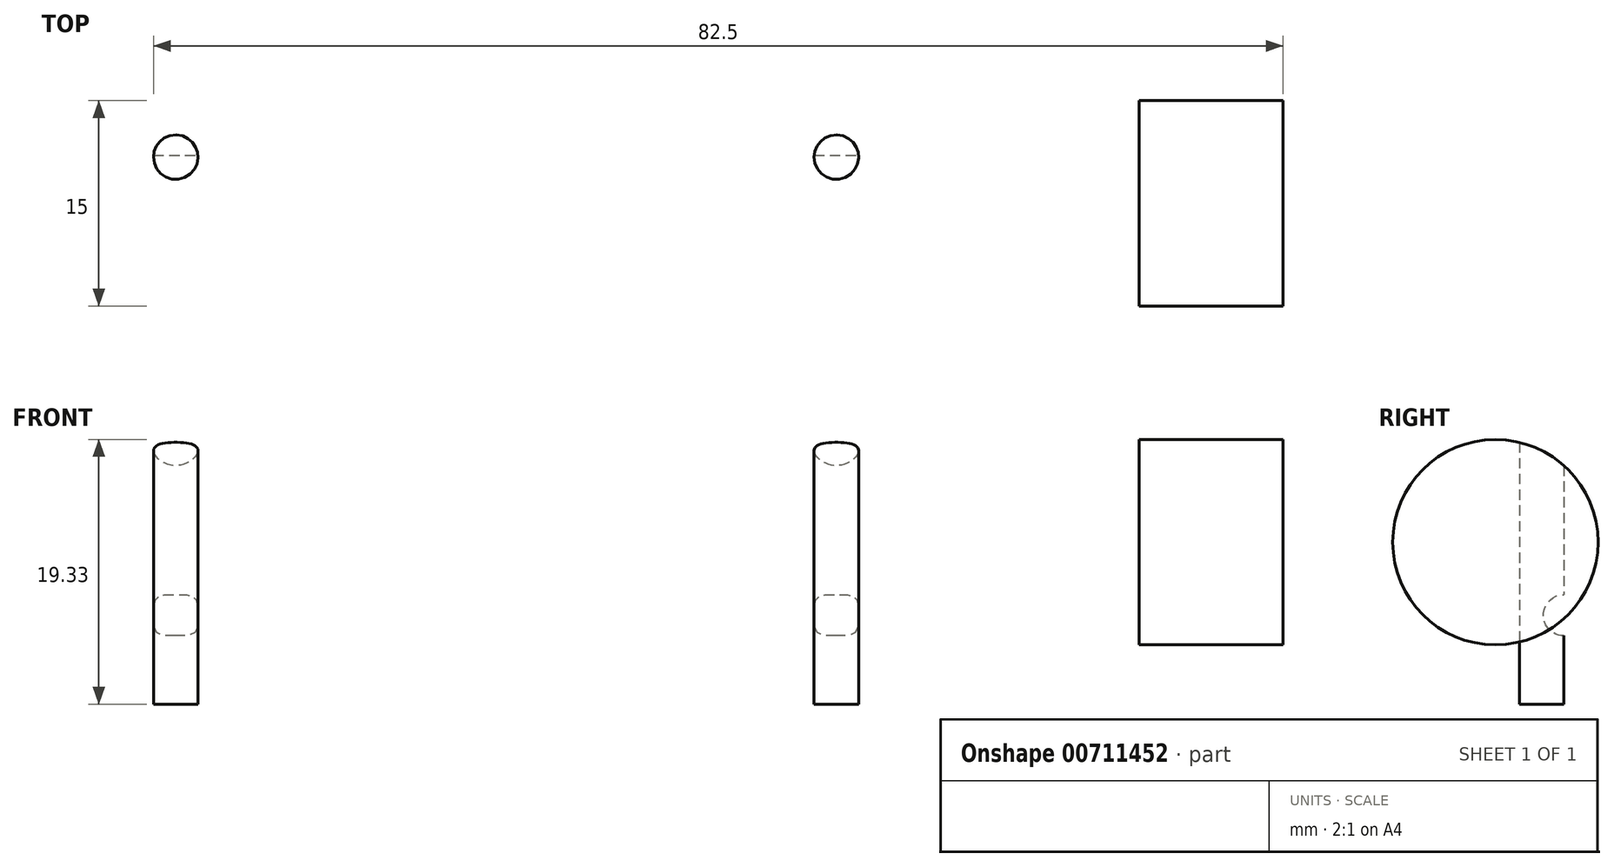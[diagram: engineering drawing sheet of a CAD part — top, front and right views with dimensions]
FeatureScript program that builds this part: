
annotation { "Feature Type Name" : "Feature", "Feature Type Description" : "" }
export const myFeature = defineFeature(function(context is Context, id is Id, definition is map)
    precondition{}
    {
        {
            var Q0;
            Q0=qCreatedBy(makeId("Top.planeOp"),FACE);
            var sketch = newSketch(context, id + "F0", { "sketchPlane" : qUnion([Q0])});
            skLineSegment(sketch, "E0.bottom", {"start": v(-41.74, -4.4) * mm, "end": v(51.26, -4.4) * mm});
            skLineSegment(sketch, "E0.top", {"start": v(-41.74, -19.4) * mm, "end": v(51.26, -19.4) * mm});
            skLineSegment(sketch, "E0.left", {"start": v(-41.74, -4.4) * mm, "end": v(-41.74, -19.4) * mm});
            skLineSegment(sketch, "E0.right", {"start": v(51.26, -4.4) * mm, "end": v(51.26, -19.4) * mm});
            skSolve(sketch);
        }
        {
            var Q0;
            Q0=makeQuery(id+"F0.imprint","IMPRINT",FACE,{"disambiguationData":[TD([[makeQuery(id+"F0.imprint","IMPRINT",EDGE,{"derivedFrom":sQuery(id+"F0.wireOp",EDGE,"E0.bottom")}),-1.0]])]});
            extrude(context, id + "F1", {"entities" : qUnion([Q0]), "depth" : 1.5 * mm, "offsetDistance" : 25 * mm});
        }
        {
            var Q0;
            Q0=makeQuery(id+"F1.opExtrude","CAP_FACE",FACE,{"disambiguationData":[OSD([sQuery(id+"F0.wireOp",EDGE,"E0.bottom"),sQuery(id+"F0.wireOp",EDGE,"E0.top"),sQuery(id+"F0.wireOp",EDGE,"E0.left"),sQuery(id+"F0.wireOp",EDGE,"E0.right")])],"isStart":false});
            var sketch = newSketch(context, id + "F2", { "sketchPlane" : qUnion([Q0])});
            skLineSegment(sketch, "E1.bottom", {"start": v(-41.74, -4.4) * mm, "end": v(-40.24, -4.4) * mm});
            skLineSegment(sketch, "E1.top", {"start": v(-41.74, -19.4) * mm, "end": v(-40.24, -19.4) * mm});
            skLineSegment(sketch, "E1.left", {"start": v(-41.74, -4.4) * mm, "end": v(-41.74, -19.4) * mm});
            skLineSegment(sketch, "E1.right", {"start": v(-40.24, -4.4) * mm, "end": v(-40.24, -19.4) * mm});
            skLineSegment(sketch, "E2.bottom", {"start": v(51.26, -4.4) * mm, "end": v(49.76, -4.4) * mm});
            skLineSegment(sketch, "E2.top", {"start": v(51.26, -19.4) * mm, "end": v(49.76, -19.4) * mm});
            skLineSegment(sketch, "E2.left", {"start": v(51.26, -4.4) * mm, "end": v(51.26, -19.4) * mm});
            skLineSegment(sketch, "E2.right", {"start": v(49.76, -4.4) * mm, "end": v(49.76, -19.4) * mm});
            skSolve(sketch);
        }
        {
            var Q0;
            Q0=makeQuery(id+"F2.imprint","IMPRINT",FACE,{"disambiguationData":[TD([[makeQuery(id+"F2.imprint","IMPRINT",EDGE,{"derivedFrom":sQuery(id+"F2.wireOp",EDGE,"E1.bottom")}),-1.0]])]});
            extrude(context, id + "F3", {"entities" : qUnion([Q0]), "operationType" : NewBodyOperationType.ADD, "depth" : 14.3 * mm, "offsetDistance" : 25 * mm});
        }
        {
            var Q0;
            Q0=makeQuery(id+"F2.imprint","IMPRINT",FACE,{"disambiguationData":[TD([[makeQuery(id+"F2.imprint","IMPRINT",EDGE,{"derivedFrom":sQuery(id+"F2.wireOp",EDGE,"E2.bottom")}),-1.0]])]});
            extrude(context, id + "F4", {"entities" : qUnion([Q0]), "operationType" : NewBodyOperationType.ADD, "depth" : 17.83 * mm, "offsetDistance" : 25 * mm});
        }
        {
            var Q0;
            Q0=makeQuery(id+"F4.boolean.opBoolean","MERGE",FACE,{"derivedFrom":[makeQuery(id+"F1.opExtrude","SWEPT_FACE",FACE,{"disambiguationData":[OSD([sQuery(id+"F0.wireOp",EDGE,"E0.right")])]}),makeQuery(id+"F4.opExtrude","SWEPT_FACE",FACE,{"disambiguationData":[OSD([sQuery(id+"F2.wireOp",EDGE,"E2.left")])]})]});
            var sketch = newSketch(context, id + "F5", { "sketchPlane" : qUnion([Q0])});
            skCircle(sketch, "E3", {"center": v(-11.9, 11.83) * mm, "radius": 7.5 * mm});
            skPoint(sketch, "E3.centerSnap0", {"position": v(-11.9, 19.33) * mm});
            skSolve(sketch);
        }
        {
            var Q0;
            {var subQ0=sQuery(id+"F5.wireOp",EDGE,"E3");var subQ1=sQuery(id+"F2.wireOp",EDGE,"E2.left");var subQ2=makeQuery(id+"F5.imprint","INTERSECT",VERTEX,{"derivedFrom":[makeQuery(id+"F4.opExtrude","CAP_EDGE",EDGE,{"disambiguationData":[OSD([subQ1])],"isStart":false}),subQ0]});Q0=makeQuery(id+"F5.imprint","IMPRINT",FACE,{"disambiguationData":[TD([[makeQuery(id+"F5.imprint","IMPRINT",EDGE,{"disambiguationData":[TD([[subQ2,1.0]])],"derivedFrom":subQ0}),1.0]])]});}
            extrude(context, id + "F6", {"entities" : qUnion([Q0]), "operationType" : NewBodyOperationType.ADD, "depth" : (12 - 1.5) * mm, "offsetDistance" : 25 * mm});
        }
        {
            var Q0;
            {var subQ0=sQuery(id+"F2.wireOp",EDGE,"E2.bottom");var subQ1=makeQuery(id+"F1.opExtrude","SWEPT_FACE",FACE,{"disambiguationData":[OSD([sQuery(id+"F0.wireOp",EDGE,"E0.right")])]});var subQ2=sQuery(id+"F2.wireOp",EDGE,"E2.left");var subQ3=makeQuery(id+"F4.opExtrude","SWEPT_FACE",FACE,{"disambiguationData":[OSD([subQ2])]});Q0=makeQuery(id+"F6.boolean.opBoolean","SPLIT",FACE,{"disambiguationData":[TD([makeQuery(id+"F1.opExtrude","SWEPT_FACE",FACE,{"disambiguationData":[OSD([sQuery(id+"F0.wireOp",EDGE,"E0.bottom")])]}),subQ1,makeQuery(id+"F3.opExtrude","SWEPT_FACE",FACE,{"disambiguationData":[OSD([sQuery(id+"F2.wireOp",EDGE,"E1.bottom")])]}),makeQuery(id+"F4.opExtrude","SWEPT_FACE",FACE,{"disambiguationData":[OSD([subQ0])]}),makeQuery(id+"F4.opExtrude","CAP_FACE",FACE,{"disambiguationData":[OSD([subQ0,sQuery(id+"F2.wireOp",EDGE,"E2.top"),subQ2,sQuery(id+"F2.wireOp",EDGE,"E2.right")])],"isStart":false}),subQ3,makeQuery(id+"F6.opExtrude","SWEPT_FACE",FACE,{"disambiguationData":[OSD([sQuery(id+"F5.wireOp",EDGE,"E3")])]})])],"derivedFrom":makeQuery(id+"F4.boolean.opBoolean","MERGE",FACE,{"derivedFrom":[subQ1,subQ3]})});}
            var Q1;
            {var subQ0=sQuery(id+"F2.wireOp",EDGE,"E2.left");var subQ1=sQuery(id+"F2.wireOp",EDGE,"E2.top");var subQ2=makeQuery(id+"F1.opExtrude","SWEPT_FACE",FACE,{"disambiguationData":[OSD([sQuery(id+"F0.wireOp",EDGE,"E0.right")])]});var subQ3=makeQuery(id+"F4.opExtrude","SWEPT_FACE",FACE,{"disambiguationData":[OSD([subQ0])]});Q1=makeQuery(id+"F6.boolean.opBoolean","SPLIT",FACE,{"disambiguationData":[TD([makeQuery(id+"F1.opExtrude","SWEPT_FACE",FACE,{"disambiguationData":[OSD([sQuery(id+"F0.wireOp",EDGE,"E0.top")])]}),subQ2,makeQuery(id+"F3.opExtrude","SWEPT_FACE",FACE,{"disambiguationData":[OSD([sQuery(id+"F2.wireOp",EDGE,"E1.top")])]}),makeQuery(id+"F4.opExtrude","CAP_FACE",FACE,{"disambiguationData":[OSD([sQuery(id+"F2.wireOp",EDGE,"E2.bottom"),subQ1,subQ0,sQuery(id+"F2.wireOp",EDGE,"E2.right")])],"isStart":false}),makeQuery(id+"F4.opExtrude","SWEPT_FACE",FACE,{"disambiguationData":[OSD([subQ1])]}),subQ3,makeQuery(id+"F6.opExtrude","SWEPT_FACE",FACE,{"disambiguationData":[OSD([sQuery(id+"F5.wireOp",EDGE,"E3")])]})])],"derivedFrom":makeQuery(id+"F4.boolean.opBoolean","MERGE",FACE,{"derivedFrom":[subQ2,subQ3]})});}
            extrude(context, id + "F7", {"entities" : qUnion([Q0, Q1]), "operationType" : NewBodyOperationType.REMOVE, "endBound" : BoundingType.UP_TO_NEXT, "oppositeDirection" : true, "depth" : 25 * mm, "offsetDistance" : 25 * mm});
        }
        {
            var Q0;
            Q0=makeQuery(id+"F4.opExtrude","SWEPT_FACE",FACE,{"disambiguationData":[OSD([sQuery(id+"F2.wireOp",EDGE,"E2.right")])]});
            var sketch = newSketch(context, id + "F8", { "sketchPlane" : qUnion([Q0])});
            skCircle(sketch, "E4", {"center": v(11.9, 11.83) * mm, "radius": 1.45 * mm});
            skLineSegment(sketch, "E5", {"start": v(11.9, 19.33) * mm, "end": v(11.9, 1.5) * mm, "construction": true});
            skCircle(sketch, "E6", {"center": v(16.9, 6.5) * mm, "radius": 1.5 * mm});
            skCircle(sketch, "E7.MirrorC", {"center": v(6.9, 6.5) * mm, "radius": 1.5 * mm});
            skSolve(sketch);
        }
        {
            var Q0;
            Q0=makeQuery(id+"F8.imprint","IMPRINT",FACE,{"disambiguationData":[TD([[makeQuery(id+"F8.imprint","IMPRINT",EDGE,{"derivedFrom":sQuery(id+"F8.wireOp",EDGE,"E7.MirrorC")}),-1.0]])]});
            var Q1;
            Q1=makeQuery(id+"F8.imprint","IMPRINT",FACE,{"disambiguationData":[TD([[makeQuery(id+"F8.imprint","IMPRINT",EDGE,{"derivedFrom":sQuery(id+"F8.wireOp",EDGE,"E4")}),1.0]])]});
            var Q2;
            Q2=makeQuery(id+"F8.imprint","IMPRINT",FACE,{"disambiguationData":[TD([[makeQuery(id+"F8.imprint","IMPRINT",EDGE,{"derivedFrom":sQuery(id+"F8.wireOp",EDGE,"E6")}),1.0]])]});
            var Q3;
            Q3=makeQuery(id+"F3.opExtrude","SWEPT_FACE",FACE,{"disambiguationData":[OSD([sQuery(id+"F2.wireOp",EDGE,"E1.right")])]});
            extrude(context, id + "F9", {"entities" : qUnion([Q0, Q1, Q2]), "operationType" : NewBodyOperationType.ADD, "endBound" : BoundingType.UP_TO_SURFACE, "depth" : 25 * mm, "endBoundEntityFace" : qUnion([Q3]), "offsetDistance" : 25 * mm});
        }
        {
            var Q0;
            Q0=makeQuery(id+"F1.opExtrude","CAP_FACE",FACE,{"disambiguationData":[OSD([sQuery(id+"F0.wireOp",EDGE,"E0.bottom"),sQuery(id+"F0.wireOp",EDGE,"E0.top"),sQuery(id+"F0.wireOp",EDGE,"E0.left"),sQuery(id+"F0.wireOp",EDGE,"E0.right")])],"isStart":true});
            var sketch = newSketch(context, id + "F10", { "sketchPlane" : qUnion([Q0])});
            skCircle(sketch, "E8", {"center": v(-19.12, 15.27) * mm, "radius": 1.62 * mm});
            skCircle(sketch, "E9", {"center": v(29.13, 15.27) * mm, "radius": 1.63 * mm});
            skLineSegment(sketch, "E10", {"start": v(-41.74, 11.9) * mm, "end": v(51.26, 11.9) * mm, "construction": true});
            skCircle(sketch, "E11.MirrorC", {"center": v(29.13, 8.52) * mm, "radius": 1.63 * mm});
            skCircle(sketch, "E12.MirrorC", {"center": v(-19.12, 8.52) * mm, "radius": 1.62 * mm});
            skSolve(sketch);
        }
        {
            var Q0;
            Q0=makeQuery(id+"F10.imprint","IMPRINT",FACE,{"disambiguationData":[TD([[makeQuery(id+"F10.imprint","IMPRINT",EDGE,{"derivedFrom":sQuery(id+"F10.wireOp",EDGE,"E8")}),1.0]])]});
            var Q1;
            Q1=makeQuery(id+"F10.imprint","IMPRINT",FACE,{"disambiguationData":[TD([[makeQuery(id+"F10.imprint","IMPRINT",EDGE,{"derivedFrom":sQuery(id+"F10.wireOp",EDGE,"E12.MirrorC")}),-1.0]])]});
            var Q2;
            Q2=makeQuery(id+"F10.imprint","IMPRINT",FACE,{"disambiguationData":[TD([[makeQuery(id+"F10.imprint","IMPRINT",EDGE,{"derivedFrom":sQuery(id+"F10.wireOp",EDGE,"E11.MirrorC")}),-1.0]])]});
            var Q3;
            Q3=makeQuery(id+"F10.imprint","IMPRINT",FACE,{"disambiguationData":[TD([[makeQuery(id+"F10.imprint","IMPRINT",EDGE,{"derivedFrom":sQuery(id+"F10.wireOp",EDGE,"E9")}),1.0]])]});
            extrude(context, id + "F11", {"entities" : qUnion([Q0, Q1, Q2, Q3]), "operationType" : NewBodyOperationType.REMOVE, "endBound" : BoundingType.UP_TO_NEXT, "oppositeDirection" : true, "depth" : 25 * mm, "offsetDistance" : 25 * mm});
        }
    });
